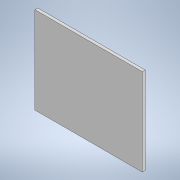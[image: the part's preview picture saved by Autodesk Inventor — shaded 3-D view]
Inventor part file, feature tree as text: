
AUTODESK INVENTOR PART (.ipt)
format: ipt  version: 2020.2 (Build 242310000, 310)  size: 92,160 bytes
history: native  units: mm
features: extrude x1, sketch x1
ambient origin geometry x8: Origin, YZ Plane, XZ Plane, XY Plane, X Axis, Y Axis, Z Axis, Center Point
bodies: Solide1 (feature_tree)
feature tree (2):
  extrude  "Extrusion1"  Depth=148.0mm
  sketch  "Esquisse1"
